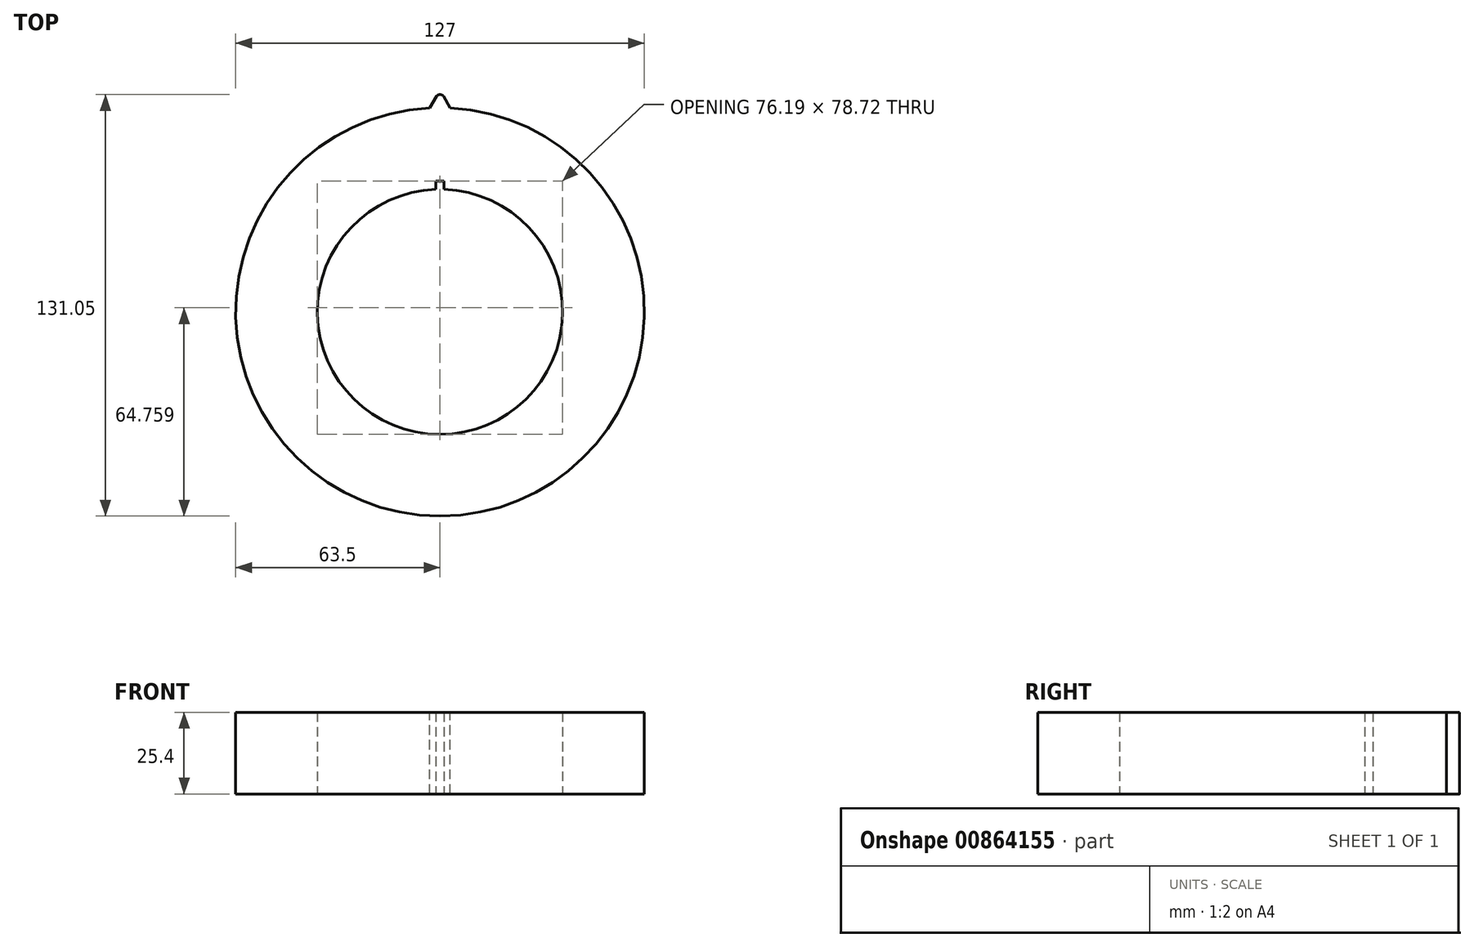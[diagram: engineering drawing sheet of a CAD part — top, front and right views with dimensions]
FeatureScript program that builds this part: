
annotation { "Feature Type Name" : "Feature", "Feature Type Description" : "" }
export const myFeature = defineFeature(function(context is Context, id is Id, definition is map)
    precondition{}
    {
        {
            var Q0;
            Q0=qCreatedBy(makeId("Top.planeOp"),FACE);
            var sketch = newSketch(context, id + "F0", { "sketchPlane" : qUnion([Q0])});
            skCircle(sketch, "E0", {"center": v(0, 0) * mm, "radius": 63.5 * mm});
            skLineSegment(sketch, "E1", {"start": v(0, 0) * mm, "end": v(0, 74.42) * mm, "construction": true});
            skLineSegment(sketch, "E2", {"start": v(0, 0) * mm, "end": v(86.35, 0) * mm, "construction": true});
            skCircle(sketch, "E3", {"center": v(0, 0) * mm, "radius": 38.1 * mm});
            skLineSegment(sketch, "E4", {"start": v(-1.27, 38.08) * mm, "end": v(-1.27, 40.62) * mm});
            skLineSegment(sketch, "E5", {"start": v(-1.27, 40.62) * mm, "end": v(1.27, 40.62) * mm});
            skLineSegment(sketch, "E6", {"start": v(1.27, 40.62) * mm, "end": v(1.27, 38.08) * mm});
            skSolve(sketch);
        }
        {
            var Q0;
            Q0 = qSketchRegion(id + "F0", true);
            extrude(context, id + "F1", {"entities" : qUnion([Q0]), "depth" : 25.4 * mm, "offsetDistance" : 25.4 * mm});
        }
        {
            var Q0;
            Q0=makeQuery(id+"F1.opExtrude","CAP_FACE",FACE,{"disambiguationData":[OSD([sQuery(id+"F0.wireOp",EDGE,"E0"),sQuery(id+"F0.wireOp",EDGE,"E3"),sQuery(id+"F0.wireOp",EDGE,"E4"),sQuery(id+"F0.wireOp",EDGE,"E5"),sQuery(id+"F0.wireOp",EDGE,"E6")])],"isStart":false});
            var sketch = newSketch(context, id + "F2", { "sketchPlane" : qUnion([Q0])});
            skLineSegment(sketch, "E7", {"start": v(-3.18, 63.42) * mm, "end": v(-0.8, 67.55) * mm});
            skLineSegment(sketch, "E8", {"start": v(-0.8, 67.55) * mm, "end": v(0.79, 67.55) * mm});
            skLineSegment(sketch, "E9", {"start": v(0.79, 67.55) * mm, "end": v(3.17, 63.42) * mm});
            skLineSegment(sketch, "E10", {"start": v(-3.18, 63.42) * mm, "end": v(3.17, 63.42) * mm});
            skSolve(sketch);
        }
        {
            var Q0;
            Q0 = qSketchRegion(id + "F2", true);
            extrude(context, id + "F3", {"entities" : qUnion([Q0]), "operationType" : NewBodyOperationType.ADD, "oppositeDirection" : true, "depth" : 25.4 * mm, "offsetDistance" : 25.4 * mm});
        }
        {
            var Q0;
            Q0=makeQuery(id+"F3.opExtrude","SWEPT_EDGE",EDGE,{"disambiguationData":[OSD([sQuery(id+"F2.wireOp",EDGE,"E7"),sQuery(id+"F2.wireOp",EDGE,"E8")])]});
            var Q1;
            Q1=makeQuery(id+"F3.opExtrude","SWEPT_EDGE",EDGE,{"disambiguationData":[OSD([sQuery(id+"F2.wireOp",EDGE,"E8"),sQuery(id+"F2.wireOp",EDGE,"E9")])]});
            fillet(context, id + "F4", {"entities" : qUnion([Q0, Q1]), "radius" : 1.02 * mm, "tangentPropagation" : true, "allowEdgeOverflow" : false});
        }
    });
